# Revit family: HC_Valve_Radiator_MEPcontent_Oventrop_QV_Straight Pattern
name_source: partatom
category: Pipe Accessories
revit_build: Autodesk Revit 2015 (Build: 20140223_1515(x64)
units: mm (PartAtom-declared; Revit-internal decimal feet)

## types (3) — shared parameters
Article Description = Automatic thermostatic radiator valve, straight pattern
Black = Color RGB 035-035-035
Brass = Color RGB 168-128-048
Cast Iron = Color RGB 140-140-140
Content Supplier URL = www.mepcontent.eu
Custom = No
Description = Automatic thermostatic radiator valve, straight pattern
EMCS Version = 2.0
ETIM Article Class = EC010136
Family Version = 10.14
IFCExportAs = IfcValveType
IFCExportType = REGULATING
Kvs Value = 0.67
MEPcontent Class = VALVE_RADIATOR
Manufacturer = Oventrop
Manufacturer URL = http://www.oventrop.de
Pressure Stage = 10.0 Pa
Product Line = Oventrop
Revit Version = 2015
Rind Height = 14.5 mm  [stored 0.0475722 ft]
Ring Vizibility = Yes
URL = www.stabiplan.com
Use Nominal Diameter = Yes
Valve Body Radius = 12.5 mm  [stored 0.0410105 ft]
Valve Insert Diameter = 30 mm  [stored 0.0984252 ft]

## per-type parameters (varying)
- DN 10: Blend Position=16 mm  [stored 0.0524934 ft]; Bottom Height=22 mm  [stored 0.0721785 ft]; Bottom Part Radius=10 mm  [stored 0.0328084 ft]; Connection Piece Radius=8 mm  [stored 0.0262467 ft]; Copper Connection Diameter=12 mm  [stored 0.0393701 ft]; Copper Connection Radius=6 mm  [stored 0.019685 ft]; GTIN=04026755416138; Height=47 mm; Horizontal Nut Diameter1=27 mm  [stored 0.0885827 ft]; Horizontal Nut Height1=13.5 mm  [stored 0.0442913 ft]; Horizontal Nut Height2=14 mm  [stored 0.0459318 ft]; Horizontal Nut Position=20 mm  [stored 0.0656168 ft]; Horizontall Nut Diameter2=25.5 mm; Left Side Length=33 mm  [stored 0.108268 ft]; Length=85 mm; Manufacturer Art. No.=1183163; Middle Section Radius=10 mm  [stored 0.0328084 ft]; Ring Position=19 mm  [stored 0.062336 ft]; Ring Radius=13 mm  [stored 0.0426509 ft]; Thread Connection Diameter=9.5 mm  [stored 0.031168 ft]; Thread Connection Nominal Diameter=9.5 mm  [stored 0.031168 ft]; Thread Connection Nominal Radius=4.75 mm  [stored 0.015584 ft]; Thread Connection Outer Diameter=17.2 mm; Thread Connection Outer Radius=8.6 mm; Valve Body Height=26 mm
- DN 15: Blend Position=17 mm  [stored 0.0557743 ft]; Bottom Height=26 mm; Bottom Part Radius=11.5 mm  [stored 0.0377297 ft]; Connection Piece Radius=10.5 mm  [stored 0.0344488 ft]; Copper Connection Diameter=15 mm  [stored 0.0492126 ft]; Copper Connection Radius=7.5 mm  [stored 0.0246063 ft]; GTIN=04026755416145; Height=47 mm; Horizontal Nut Diameter1=30 mm  [stored 0.0984252 ft]; Horizontal Nut Height1=15 mm  [stored 0.0492126 ft]; Horizontal Nut Height2=15 mm  [stored 0.0492126 ft]; Horizontal Nut Position=23 mm  [stored 0.0754593 ft]; Horizontall Nut Diameter2=30 mm  [stored 0.0984252 ft]; Left Side Length=36 mm  [stored 0.11811 ft]; Length=95 mm; Manufacturer Art. No.=1183164; Middle Section Radius=11 mm  [stored 0.0360892 ft]; Ring Position=23 mm  [stored 0.0754593 ft]; Ring Radius=13 mm  [stored 0.0426509 ft]; Thread Connection Diameter=12.7 mm  [stored 0.0416667 ft]; Thread Connection Nominal Diameter=12.7 mm  [stored 0.0416667 ft]; Thread Connection Nominal Radius=6.35 mm  [stored 0.0208333 ft]; Thread Connection Outer Diameter=21.3 mm  [stored 0.0698819 ft]; Thread Connection Outer Radius=10.65 mm  [stored 0.0349409 ft]; Valve Body Height=26 mm
- DN 20: Blend Position=19 mm  [stored 0.062336 ft]; Bottom Height=29 mm  [stored 0.0951444 ft]; Bottom Part Radius=13 mm  [stored 0.0426509 ft]; Connection Piece Radius=13 mm  [stored 0.0426509 ft]; Copper Connection Diameter=22 mm  [stored 0.0721785 ft]; Copper Connection Radius=11 mm  [stored 0.0360892 ft]; GTIN=04026755416152; Height=45 mm; Horizontal Nut Diameter1=37 mm  [stored 0.121391 ft]; Horizontal Nut Height1=16.5 mm  [stored 0.0541339 ft]; Horizontal Nut Height2=17 mm  [stored 0.0557743 ft]; Horizontal Nut Position=23.5 mm  [stored 0.0770997 ft]; Horizontall Nut Diameter2=37 mm  [stored 0.121391 ft]; Left Side Length=43 mm; Length=106 mm; Manufacturer Art. No.=1183166; Middle Section Radius=14 mm  [stored 0.0459318 ft]; Ring Position=27 mm  [stored 0.0885827 ft]; Ring Radius=14 mm  [stored 0.0459318 ft]; Thread Connection Diameter=19 mm  [stored 0.062336 ft]; Thread Connection Nominal Diameter=19 mm  [stored 0.062336 ft]; Thread Connection Nominal Radius=9.5 mm  [stored 0.031168 ft]; Thread Connection Outer Diameter=26.9 mm; Thread Connection Outer Radius=13.45 mm; Valve Body Height=27 mm  [stored 0.0885827 ft]

note: column(s) folded — value = type name in every type: Article Type, Model

note: [stored X ft] marks values corroborated as IEEE doubles in the binary element streams (Revit-internal decimal feet)

## geometry (parser evidence)
native form markers: Blend x1, Sweep x7
no freeform markers — native parametric forms only
